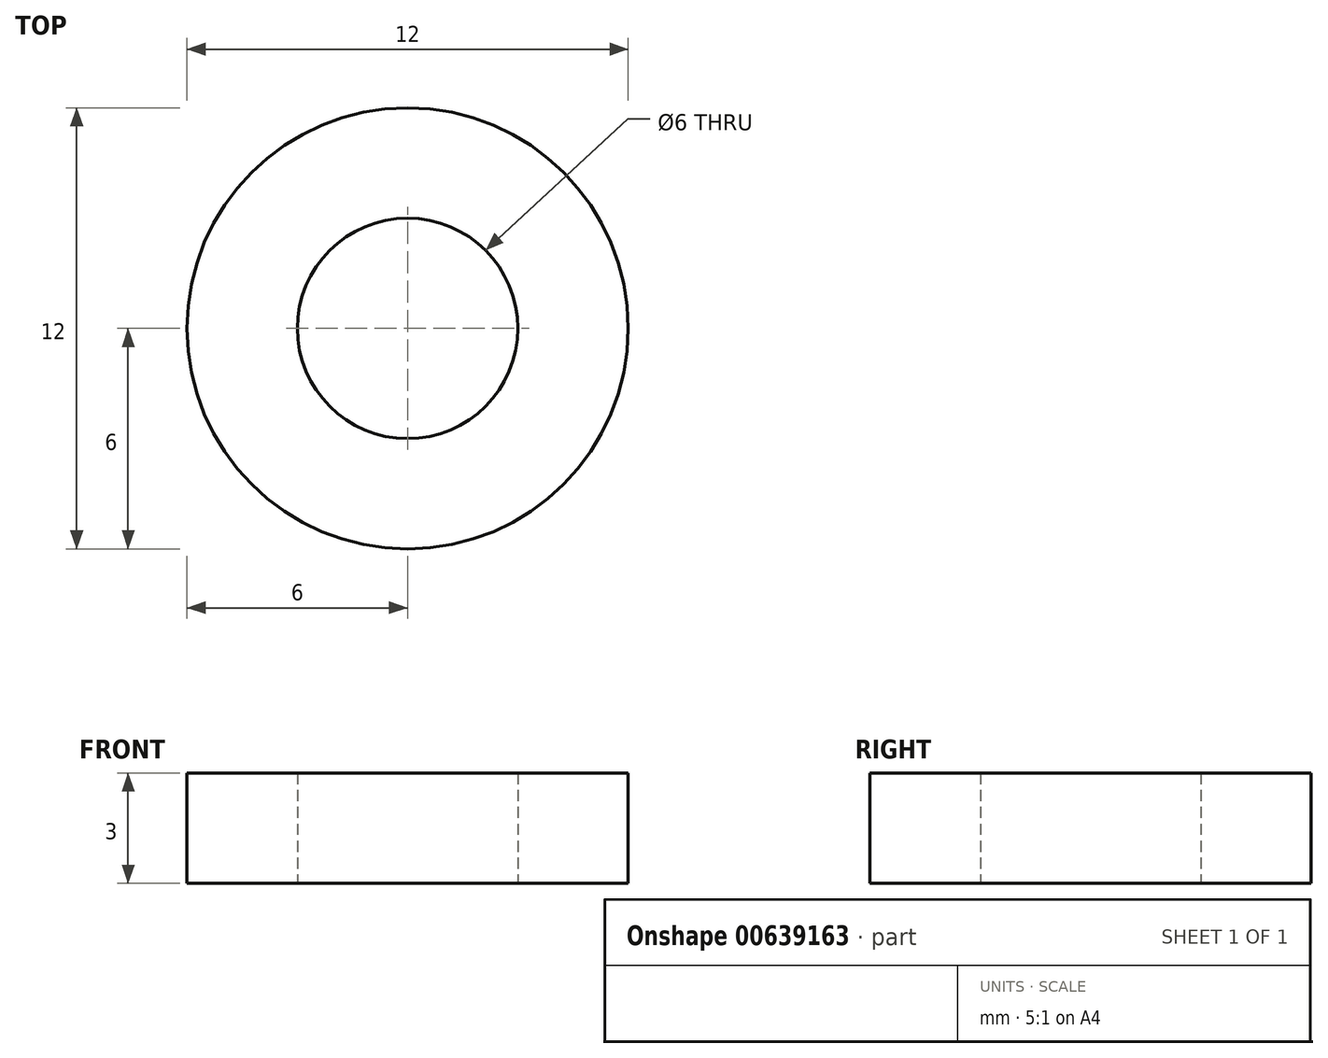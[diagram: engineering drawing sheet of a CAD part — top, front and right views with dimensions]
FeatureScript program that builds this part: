
annotation { "Feature Type Name" : "Feature", "Feature Type Description" : "" }
export const myFeature = defineFeature(function(context is Context, id is Id, definition is map)
    precondition{}
    {
        {
            var Q0;
            Q0=qCreatedBy(makeId("Top.planeOp"),FACE);
            var sketch = newSketch(context, id + "F0", { "sketchPlane" : qUnion([Q0])});
            skCircle(sketch, "E0", {"center": v(0, 0) * mm, "radius": 3 * mm});
            skCircle(sketch, "E1", {"center": v(0, 0) * mm, "radius": 6 * mm});
            skSolve(sketch);
        }
        {
            var Q0;
            Q0=makeQuery(id+"F0.imprint","IMPRINT",FACE,{"disambiguationData":[TD([[makeQuery(id+"F0.imprint","IMPRINT",EDGE,{"derivedFrom":sQuery(id+"F0.wireOp",EDGE,"E0")}),-1.0]])]});
            extrude(context, id + "F1", {"entities" : qUnion([Q0]), "depth" : 3 * mm, "offsetDistance" : 25 * mm});
        }
    });
